# Revit family: Shower-Receptor-Sterling-Guard-72331100
name_source: partatom
category: Plumbing Fixtures
revit_build: Autodesk Revit 2015 (Build: 20140606_1530(x64)
units: mm (PartAtom-declared; Revit-internal decimal feet)

## types (2) — shared parameters
ADA Compliant = Yes
Assembly Code = C1030200
Date Modified = 09/18/2017
Default Elevation = 0"
Description = GUARD+™60 inch Shower Base
Flow Rate = 0 GPM
Height = 4 3/16"
Inlet Connection = Inlet Connection
Length = 60"
Manufacturer = Sterling
MasterFormat 1995 = 15410
MasterFormat 2004 = 22.41.23
Material = Vikrell® material.
Outlet Connection = Outlet Connection
Pressure = 0.00 psi
Product Documentation Link = https://www.sterlingplumbing.com
Product Name = GUARD+
Product Page URL = http://www.sterlingplumbing.com
URL = https://www.sterlingplumbing.com
Width = 34"

## per-type parameters (varying)
| type | Finish | Model | Type | Waste Connection |
| 60"-0-White | China - Kohler - 0 - White | 72331100-0-White | 1 | Yes |
| 60"-96-Biscuit | China - Kohler - 96- Biscuit | 72331100-96-Biscuit | 2 | No |

## geometry (parser evidence)
native form markers: Sweep x6
no freeform markers — native parametric forms only
